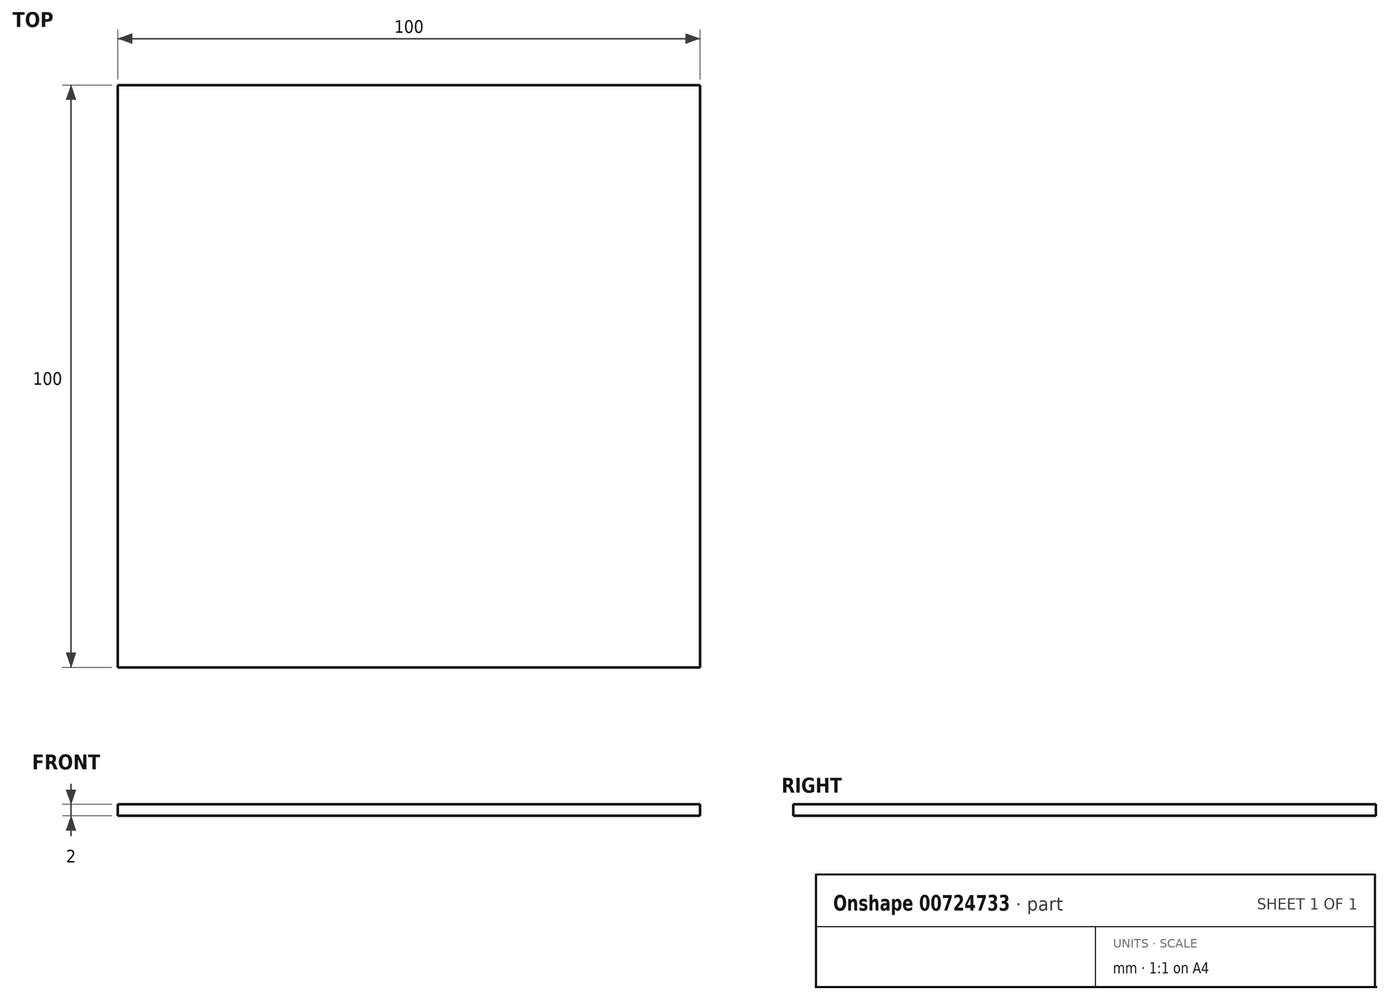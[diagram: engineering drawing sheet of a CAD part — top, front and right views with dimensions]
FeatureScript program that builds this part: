
annotation { "Feature Type Name" : "Feature", "Feature Type Description" : "" }
export const myFeature = defineFeature(function(context is Context, id is Id, definition is map)
    precondition{}
    {
        {
            var Q0;
            Q0=qCreatedBy(makeId("Top.planeOp"),FACE);
            var sketch = newSketch(context, id + "F0", { "sketchPlane" : qUnion([Q0])});
            skLineSegment(sketch, "E0.bottom", {"start": v(-50, 50) * mm, "end": v(50, 50) * mm});
            skLineSegment(sketch, "E0.top", {"start": v(-50, -50) * mm, "end": v(50, -50) * mm});
            skLineSegment(sketch, "E0.left", {"start": v(-50, 50) * mm, "end": v(-50, -50) * mm});
            skLineSegment(sketch, "E0.right", {"start": v(50, 50) * mm, "end": v(50, -50) * mm});
            skPoint(sketch, "E0.middle", {"position": v(0, 0) * mm});
            skSolve(sketch);
        }
        {
            var Q0;
            Q0=makeQuery(id+"F0.imprint","IMPRINT",FACE,{"disambiguationData":[TD([[makeQuery(id+"F0.imprint","IMPRINT",EDGE,{"derivedFrom":sQuery(id+"F0.wireOp",EDGE,"E0.bottom")}),-1.0]])]});
            extrude(context, id + "F1", {"entities" : qUnion([Q0]), "depth" : 2 * mm, "offsetDistance" : 25 * mm});
        }
    });
